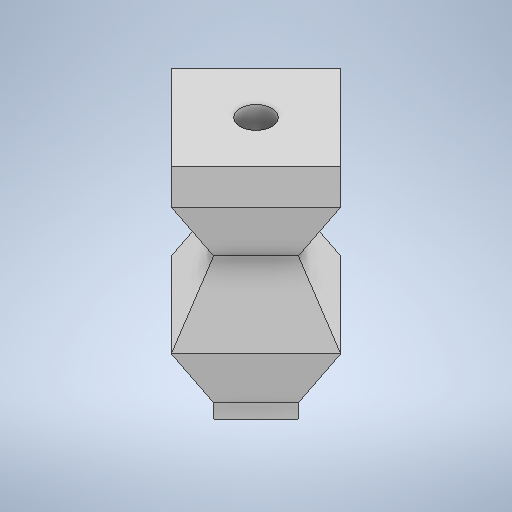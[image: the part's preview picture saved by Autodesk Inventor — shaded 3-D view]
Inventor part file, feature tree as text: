
AUTODESK INVENTOR PART (.ipt)
format: ipt  version: 2025.1 (Build 291241000, 241)  size: 283,136 bytes
history: native  units: mm
features: sketch x5, other x3, extrude x3, mirror x2, projected_geometry x2, loft x1, shell x1
ambient origin geometry x8: Origin, YZ Plane, XZ Plane, XY Plane, X Axis, Y Axis, Z Axis, Center Point
bodies: Body1 (feature_tree)
feature tree (17):
  other  "솔리드1"
  sketch  "스케치1"
  other  "작업 평면1"
  loft  "로프트1"
  other  "작업 평면2"
  mirror  "미러1"
  mirror  "미러2"
  shell  "쉘1"  Thickness=9.0mm
  extrude  "돌출1"  Depth=12.0mm
  extrude  "돌출2"  TaperAngle=0.0deg  [1 undecoded]
  extrude  "돌출3"  TaperAngle=0.0deg  [1 undecoded]
  sketch  "스케치2"
  sketch  "스케치3"
  projected_geometry  "투영된 루프1"
  sketch  "스케치4"
  projected_geometry  "투영된 루프2"
  sketch  "스케치5"
note: 2 required parameter values undecoded (feature->parameter linkage not recoverable at this tier; creation-order binding heuristic only, values carry confidence <= 0.55)
